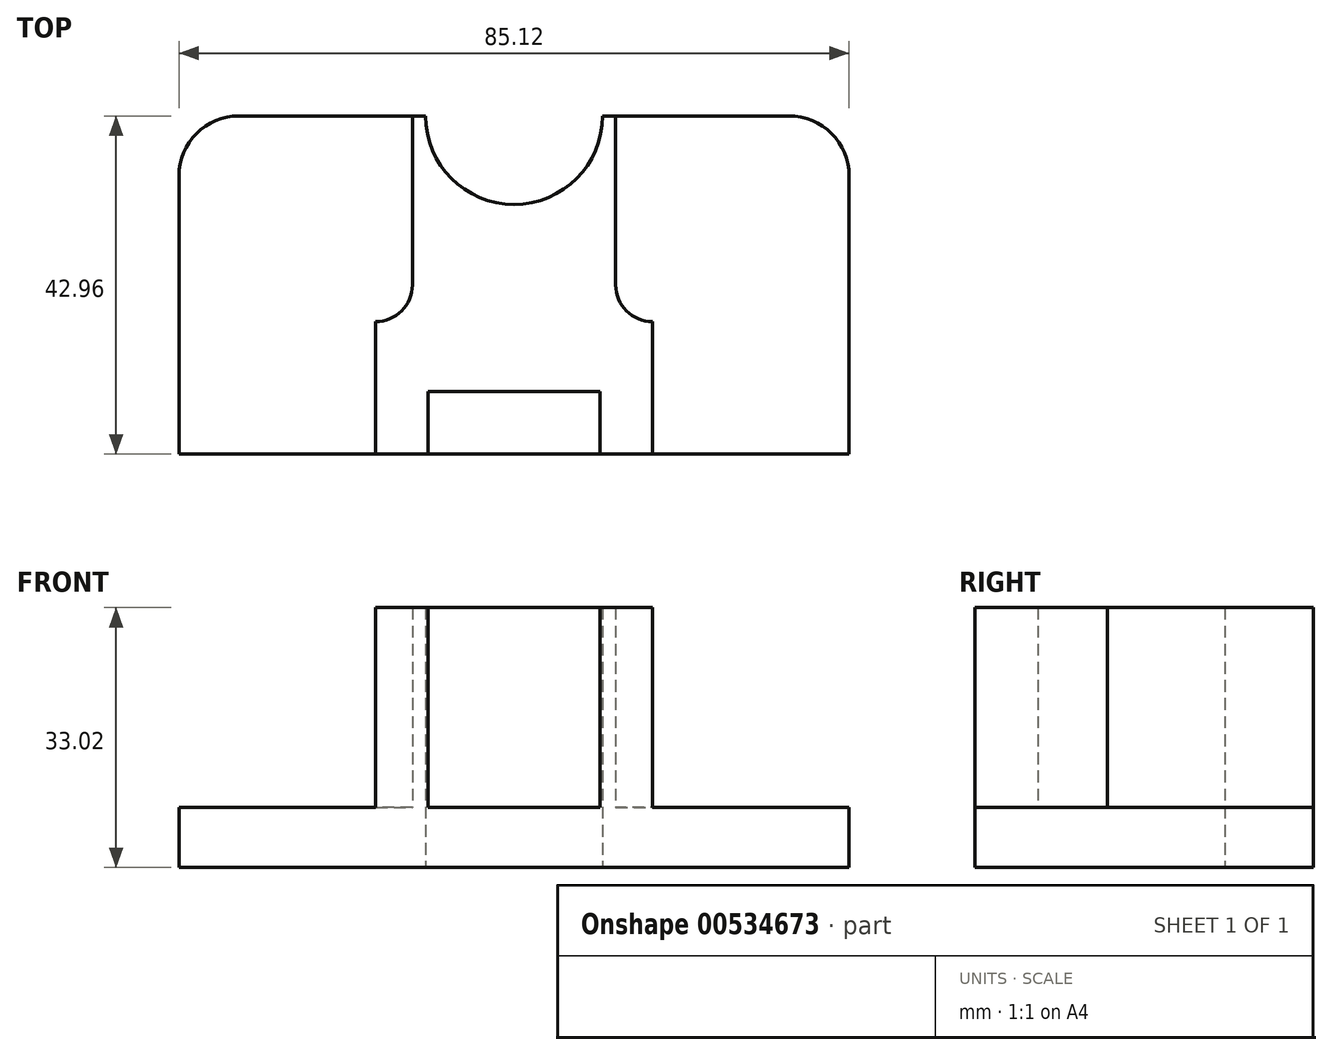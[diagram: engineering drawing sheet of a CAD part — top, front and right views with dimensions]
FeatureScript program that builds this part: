
annotation { "Feature Type Name" : "Feature", "Feature Type Description" : "" }
export const myFeature = defineFeature(function(context is Context, id is Id, definition is map)
    precondition{}
    {
        {
            var Q0;
            Q0=qCreatedBy(makeId("Top.planeOp"),FACE);
            var sketch = newSketch(context, id + "F0", { "sketchPlane" : qUnion([Q0])});
            skLineSegment(sketch, "E0.bottom", {"start": v(42.56, 21.48) * mm, "end": v(-42.56, 21.48) * mm});
            skLineSegment(sketch, "E0.top", {"start": v(42.56, -21.48) * mm, "end": v(-42.56, -21.48) * mm});
            skLineSegment(sketch, "E0.left", {"start": v(42.56, 21.48) * mm, "end": v(42.56, -21.48) * mm});
            skLineSegment(sketch, "E0.right", {"start": v(-42.56, 21.48) * mm, "end": v(-42.56, -21.48) * mm});
            skPoint(sketch, "E0.middle", {"position": v(0, 0) * mm});
            skSolve(sketch);
        }
        {
            var Q0;
            Q0 = qSketchRegion(id + "F0", true);
            extrude(context, id + "F1", {"entities" : qUnion([Q0]), "depth" : 7.62 * mm, "offsetDistance" : 25.4 * mm});
        }
        {
            var Q0;
            Q0=makeQuery(id+"F1.opExtrude","SWEPT_EDGE",EDGE,{"disambiguationData":[OSD([sQuery(id+"F0.wireOp",EDGE,"E0.bottom"),sQuery(id+"F0.wireOp",EDGE,"E0.right")])]});
            var Q1;
            Q1=makeQuery(id+"F1.opExtrude","SWEPT_EDGE",EDGE,{"disambiguationData":[OSD([sQuery(id+"F0.wireOp",EDGE,"E0.bottom"),sQuery(id+"F0.wireOp",EDGE,"E0.left")])]});
            fillet(context, id + "F2", {"entities" : qUnion([Q0, Q1]), "radius" : 7.62 * mm, "tangentPropagation" : true, "allowEdgeOverflow" : false});
        }
        {
            var Q0;
            Q0=makeQuery(id+"F1.opExtrude","CAP_FACE",FACE,{"disambiguationData":[OSD([sQuery(id+"F0.wireOp",EDGE,"E0.bottom"),sQuery(id+"F0.wireOp",EDGE,"E0.top"),sQuery(id+"F0.wireOp",EDGE,"E0.left"),sQuery(id+"F0.wireOp",EDGE,"E0.right")])],"isStart":false});
            var sketch = newSketch(context, id + "F3", { "sketchPlane" : qUnion([Q0])});
            skCircle(sketch, "E1", {"center": v(0, 21.48) * mm, "radius": 11.24 * mm});
            skLineSegment(sketch, "E2", {"start": v(11.24, 21.48) * mm, "end": v(12.92, 21.48) * mm});
            skLineSegment(sketch, "E3", {"start": v(12.92, 21.48) * mm, "end": v(12.92, 0) * mm});
            skArc(sketch, "E4", {"start": v(12.92, 0) * mm, "mid": v(14.28, -3.28) * mm, "end": v(17.56, -4.64) * mm});
            skLineSegment(sketch, "E5", {"start": v(17.56, -4.64) * mm, "end": v(17.56, -21.48) * mm});
            skLineSegment(sketch, "E6", {"start": v(17.56, -21.48) * mm, "end": v(10.94, -21.48) * mm});
            skLineSegment(sketch, "E7", {"start": v(10.94, -21.48) * mm, "end": v(10.94, -13.5) * mm});
            skLineSegment(sketch, "E8", {"start": v(10.94, -13.5) * mm, "end": v(-3.65, -13.5) * mm});
            skLineSegment(sketch, "E9.MirrorCS", {"start": v(-11.24, 21.48) * mm, "end": v(-12.92, 21.48) * mm});
            skLineSegment(sketch, "E10.MirrorCS", {"start": v(-12.92, 21.48) * mm, "end": v(-12.92, 0) * mm});
            skArc(sketch, "E11.MirrorCS", {"start": v(-12.92, 0) * mm, "mid": v(-14.28, -3.28) * mm, "end": v(-17.56, -4.64) * mm});
            skLineSegment(sketch, "E12.MirrorCS", {"start": v(-10.94, -21.48) * mm, "end": v(-10.94, -13.5) * mm});
            skLineSegment(sketch, "E13.MirrorCS", {"start": v(-17.56, -4.64) * mm, "end": v(-17.56, -21.48) * mm});
            skLineSegment(sketch, "E14.MirrorCS", {"start": v(-17.56, -21.48) * mm, "end": v(-10.94, -21.48) * mm});
            skLineSegment(sketch, "E15.MirrorCS", {"start": v(-10.94, -13.5) * mm, "end": v(3.65, -13.5) * mm});
            skSolve(sketch);
        }
        {
            var Q0;
            {var subQ2=sQuery(id+"F3.wireOp",EDGE,"E2");Q0=makeQuery(id+"F3.imprint","IMPRINT",FACE,{"disambiguationData":[TD([[makeQuery(id+"F3.imprint","IMPRINT",EDGE,{"derivedFrom":subQ2}),1.0]])]});}
            extrude(context, id + "F4", {"entities" : qUnion([Q0]), "operationType" : NewBodyOperationType.ADD, "depth" : 25.4 * mm, "offsetDistance" : 25.4 * mm});
        }
        {
            var Q0;
            {var subQ0=sQuery(id+"F0.wireOp",EDGE,"E0.bottom");Q0=makeQuery(id+"F4.boolean.opBoolean","SPLIT",FACE,{"disambiguationData":[TD([makeQuery(id+"F4.opExtrude","SWEPT_FACE",FACE,{"disambiguationData":[OSD([sQuery(id+"F3.wireOp",EDGE,"E1")])]})])],"derivedFrom":makeQuery(id+"F1.opExtrude","CAP_FACE",FACE,{"disambiguationData":[OSD([subQ0,sQuery(id+"F0.wireOp",EDGE,"E0.top"),sQuery(id+"F0.wireOp",EDGE,"E0.left"),sQuery(id+"F0.wireOp",EDGE,"E0.right")])],"isStart":false})});}
            extrude(context, id + "F5", {"entities" : qUnion([Q0]), "operationType" : NewBodyOperationType.REMOVE, "oppositeDirection" : true, "depth" : 25.4 * mm, "offsetDistance" : 25.4 * mm});
        }
    });
